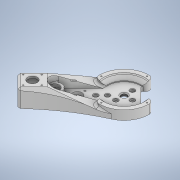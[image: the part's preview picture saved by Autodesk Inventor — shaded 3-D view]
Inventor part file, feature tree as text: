
AUTODESK INVENTOR PART (.ipt)
format: ipt  version: 2021 (Build 250183000, 183)  size: 625,664 bytes
history: native  units: mm
features: extrude x24, sketch x24, fillet x7, chamfer x7
ambient origin geometry x8: Origin, YZ Plane, XZ Plane, XY Plane, X Axis, Y Axis, Z Axis, Center Point
bodies: Solid1 (feature_tree)
feature tree (62):
  extrude  "Extrusion1"  Depth=10.0mm TaperAngle=0.0deg
  extrude  "Extrusion2"  Depth=10.0mm TaperAngle=0.0deg
  extrude  "Extrusion3"  Depth=2.0mm TaperAngle=0.0deg
  fillet  "Fillet1"  Radius=2.0mm
  chamfer  "Chamfer1"  Distance=8.0mm Angle=45.0deg
  extrude  "Extrusion4"  Depth=3.1mm
  extrude  "Extrusion5"  Depth=3.1mm
  extrude  "Extrusion6"  TaperAngle=0.0deg  [1 undecoded]
  fillet  "Fillet2"  [1 undecoded]
  extrude  "Extrusion7"  Depth=55.0mm
  extrude  "Extrusion8"  Depth=55.0mm
  chamfer  "Chamfer2"  Distance=2.0mm
  extrude  "Extrusion9"  Depth=5.5mm
  extrude  "Extrusion10"  Depth=5.5mm
  fillet  "Fillet3"  Radius=5.0mm
  extrude  "Extrusion11"  Depth=25.0mm
  chamfer  "Chamfer3"  Distance=7.0mm
  extrude  "Extrusion12"  Depth=7.0mm TaperAngle=0.0deg
  extrude  "Extrusion13"  Depth=4.1mm
  extrude  "Extrusion14"  Depth=4.1mm
  extrude  "Extrusion15"  TaperAngle=0.0deg  [1 undecoded]
  extrude  "Extrusion16"  TaperAngle=0.0deg  [1 undecoded]
  extrude  "Extrusion17"  Depth=40.0mm
  extrude  "Extrusion18"  Depth=40.0mm
  extrude  "Extrusion19"  Depth=20.0mm
  extrude  "Extrusion20"  Depth=7.0mm TaperAngle=0.0deg
  chamfer  "Chamfer4"  Distance=4.1mm
  chamfer  "Chamfer5"  Distance=20.0mm
  extrude  "Extrusion21"  Depth=20.0mm
  extrude  "Extrusion22"  Depth=4.1mm
  fillet  "Fillet5"  Radius=20.0mm
  chamfer  "Chamfer7"  Distance=10.0mm
  chamfer  "Chamfer8"  Distance=10.0mm
  fillet  "Fillet6"  Radius=10.0mm
  fillet  "Fillet7"  Radius=60.0mm
  extrude  "Extrusion24"  Depth=7.0mm TaperAngle=0.0deg
  extrude  "Extrusion26"  Depth=3.0mm
  fillet  "Fillet8"  Radius=10.0mm
  sketch  "Sketch1"  dims[d0=120.0mm d1=10.0mm d2=0.0mm]
  sketch  "Sketch2"  dims[d3=80.0mm d4=10.0mm d5=0.0mm]
  sketch  "Sketch3"  dims[d6=100.0mm d7=2.0mm d8=0.0mm d9=2.0mm d10=8.0mm d11=2.0mm d12=45.0deg]
  sketch  "Sketch4"  dims[d13=3.1mm d14=3.1mm]
  sketch  "Sketch5"  dims[d15=3.1mm d16=3.1mm]
  sketch  "Sketch6"  dims[d17=0.0mm d18=0.0mm d19=0.0mm]
  sketch  "Sketch7"  dims[d20=55.0mm d21=55.0mm]
  sketch  "Sketch8"  dims[d22=55.0mm d23=55.0mm]
  sketch  "Sketch10"  dims[d24=0.0mm d25=2.0mm d26=0.0mm]
  sketch  "Sketch12"  dims[d27=5.5mm d28=5.5mm]
  sketch  "Sketch13"  dims[d29=5.5mm d30=5.5mm d31=5.0mm d32=0.0mm]
  sketch  "Sketch14"  dims[d33=25.0mm d34=25.0mm]
  sketch  "Sketch15"  dims[d35=45.0deg]
  sketch  "Sketch16"  dims[d36=25.0mm]
  sketch  "Sketch17"  dims[d37=0.0mm]
  sketch  "Sketch18"  dims[d38=10.0mm]
  sketch  "Sketch19"  dims[d39=22.4mm d40=7.0mm d41=0.0mm]
  sketch  "Sketch20"  dims[d42=14.0mm d43=7.0mm d44=0.0mm]
  sketch  "Sketch21"  dims[d45=2.0mm d46=2.0mm d47=45.0deg d48=4.1mm]
  sketch  "Sketch23"  dims[d49=4.1mm d50=4.1mm]
  sketch  "Sketch24"  dims[d51=4.1mm d52=0.0mm]
  sketch  "Sketch25"  dims[d53=0.0mm d54=0.0mm]
  sketch  "Sketch28"  dims[d55=0.0mm d56=40.0mm]
  sketch  "Sketch31"  dims[d57=20.0mm d58=40.0mm d59=20.0mm d60=7.0mm d61=0.0mm d62=4.1mm d63=20.0mm d64=20.0mm d65=4.1mm d66=20.0mm d67=10.0mm d68=10.0mm d69=10.0mm d70=60.0mm d71=7.0mm d72=0.0mm d73=3.0mm d74=10.0mm d75=10.0mm d76=10.0mm d77=10.0mm d78=10.0mm d79=5.0mm d80=0.0mm d81=1.0mm d82=2.0mm d83=45.0deg d84=10.0mm d85=10.0mm d86=60.0mm d87=22.3mm d88=79.5mm d89=22.3mm d90=38.5mm d91=23.0mm d92=38.0mm d93=25.0mm d94=10.0mm d95=0.0mm d97=14.0mm d98=14.0mm d99=3.0mm d100=0.0mm d101=14.0mm d102=33.0mm d103=9.0mm d104=0.0mm d105=22.3mm d106=7.0mm d107=0.0mm d108=14.0mm d109=3.0mm d110=0.0mm d111=42.7mm d112=42.7mm d113=3.65mm d114=21.35mm d115=21.35mm d116=32.0mm d117=0.0mm d118=5.0mm d119=0.0mm d120=10.0mm d121=0.0mm d122=3.2mm d123=3.2mm d124=3.2mm d125=3.2mm d126=31.5mm d127=31.5mm d128=31.5mm d129=31.5mm d130=5.6mm d131=5.6mm d132=5.6mm d133=5.6mm d134=10.0mm d135=0.0mm d136=2.0mm d137=2.0mm d138=45.0deg d139=2.0mm d140=2.0mm d141=45.0deg d142=5.0mm d143=5.0mm d144=10.0mm d145=0.0mm d146=10.0mm d147=0.0mm d154=20.0mm d155=5.0mm d156=2.0mm d157=45.0deg d158=5.0mm d159=2.0mm d160=45.0deg d161=500.0mm d162=2.4mm d163=46.0mm d164=5.0mm d165=1.0mm d166=0.0mm d167=0.0mm d174=4.3mm d175=4.3mm d176=36.1mm d177=45.0deg d178=4.0mm d179=0.0mm d180=4.8mm d96=0.5mm d172=0.5mm d173=0.872665mm]
note: 4 required parameter values undecoded (feature->parameter linkage not recoverable at this tier; creation-order binding heuristic only, values carry confidence <= 0.55)
